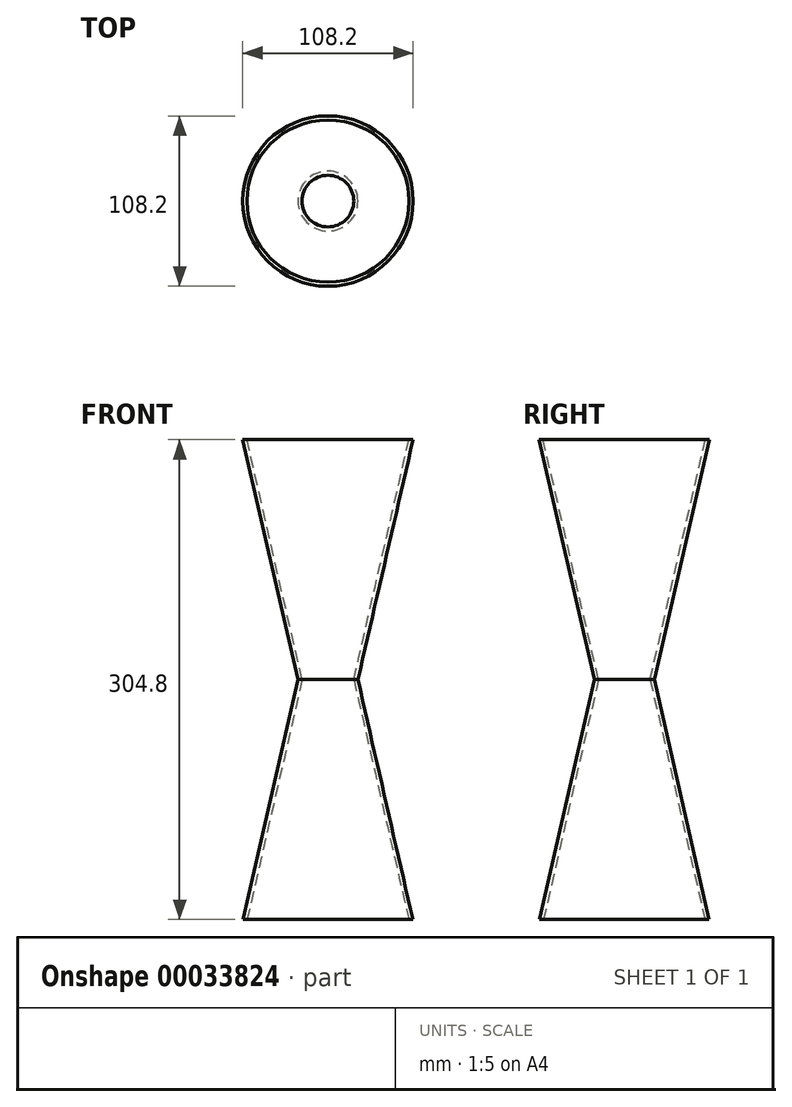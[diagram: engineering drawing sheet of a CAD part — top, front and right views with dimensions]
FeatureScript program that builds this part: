
annotation { "Feature Type Name" : "Feature", "Feature Type Description" : "" }
export const myFeature = defineFeature(function(context is Context, id is Id, definition is map)
    precondition{}
    {
        {
            var Q0;
            Q0=qCreatedBy(makeId("Top.planeOp"),FACE);
            var sketch = newSketch(context, id + "F0", { "sketchPlane" : qUnion([Q0])});
            skCircle(sketch, "E0", {"center": v(0, 0) * mm, "radius": 53.93 * mm});
            skSolve(sketch);
        }
        {
            var Q0;
            Q0=qCreatedBy(makeId("Top.planeOp"),FACE);
            cPlane(context, id + "F1", {"entities" : qUnion([Q0]), "cplaneType" : CPlaneType.OFFSET, "offset" : 152.4 * mm, "width" : 152.4 * mm, "height" : 152.4 * mm});
        }
        {
            var Q0;
            Q0=qCreatedBy(id+"F1.planeOp",FACE);
            var sketch = newSketch(context, id + "F2", { "sketchPlane" : qUnion([Q0])});
            skCircle(sketch, "E1", {"center": v(0, 0) * mm, "radius": 19.02 * mm});
            skSolve(sketch);
        }
        {
            var Q0;
            Q0=makeQuery(id+"F0.imprint","IMPRINT",FACE,{"disambiguationData":[TD([[makeQuery(id+"F0.imprint","IMPRINT",EDGE,{"derivedFrom":sQuery(id+"F0.wireOp",EDGE,"E0")}),1.0]])]});
            var Q1;
            Q1=makeQuery(id+"F2.imprint","IMPRINT",FACE,{"disambiguationData":[TD([[makeQuery(id+"F2.imprint","IMPRINT",EDGE,{"derivedFrom":sQuery(id+"F2.wireOp",EDGE,"E1")}),1.0]])]});
            loft(context, id + "F3", {"sheetProfilesArray" : [{ "sheetProfileEntities" : qUnion([Q0]) }, { "sheetProfileEntities" : qUnion([Q1]) }]});
        }
        {
            var Q0;
            Q0=qCreatedBy(id+"F1.planeOp",FACE);
            cPlane(context, id + "F4", {"entities" : qUnion([Q0]), "cplaneType" : CPlaneType.OFFSET, "offset" : 152.4 * mm, "width" : 152.4 * mm, "height" : 152.4 * mm});
        }
        {
            var Q0;
            Q0=qCreatedBy(id+"F4.planeOp",FACE);
            var sketch = newSketch(context, id + "F5", { "sketchPlane" : qUnion([Q0])});
            skCircle(sketch, "E2", {"center": v(0, 0) * mm, "radius": 54.1 * mm});
            skSolve(sketch);
        }
        {
            var Q1;
            Q1=makeQuery(id+"F3.opLoft","CAP_FACE",FACE,{"disambiguationData":[OSD([makeQuery(id+"F2.imprint","IMPRINT",FACE,{"disambiguationData":[TD([[makeQuery(id+"F2.imprint","IMPRINT",EDGE,{"derivedFrom":sQuery(id+"F2.wireOp",EDGE,"E1")}),1.0]])]})])],"isStart":true});
            var Q2;
            Q2=makeQuery(id+"F5.imprint","IMPRINT",FACE,{"disambiguationData":[TD([[makeQuery(id+"F5.imprint","IMPRINT",EDGE,{"derivedFrom":sQuery(id+"F5.wireOp",EDGE,"E2")}),1.0]])]});
            loft(context, id + "F6", {"operationType" : NewBodyOperationType.ADD, "sheetProfilesArray" : [{ "sheetProfileEntities" : qUnion([Q1]) }, { "sheetProfileEntities" : qUnion([Q2]) }]});
        }
        {
            var Q0;
            Q0=makeQuery(id+"F6.opLoft","CAP_FACE",FACE,{"disambiguationData":[OSD([makeQuery(id+"F5.imprint","IMPRINT",FACE,{"disambiguationData":[TD([[makeQuery(id+"F5.imprint","IMPRINT",EDGE,{"derivedFrom":sQuery(id+"F5.wireOp",EDGE,"E2")}),1.0]])]})])],"isStart":true});
            var Q1;
            Q1=makeQuery(id+"F3.opLoft","CAP_FACE",FACE,{"disambiguationData":[OSD([makeQuery(id+"F0.imprint","IMPRINT",FACE,{"disambiguationData":[TD([[makeQuery(id+"F0.imprint","IMPRINT",EDGE,{"derivedFrom":sQuery(id+"F0.wireOp",EDGE,"E0")}),1.0]])]})])],"isStart":true});
            shell(context, id + "F7", {"entities" : qUnion([Q0, Q1]), "thickness" : 2.54 * mm});
        }
    });
